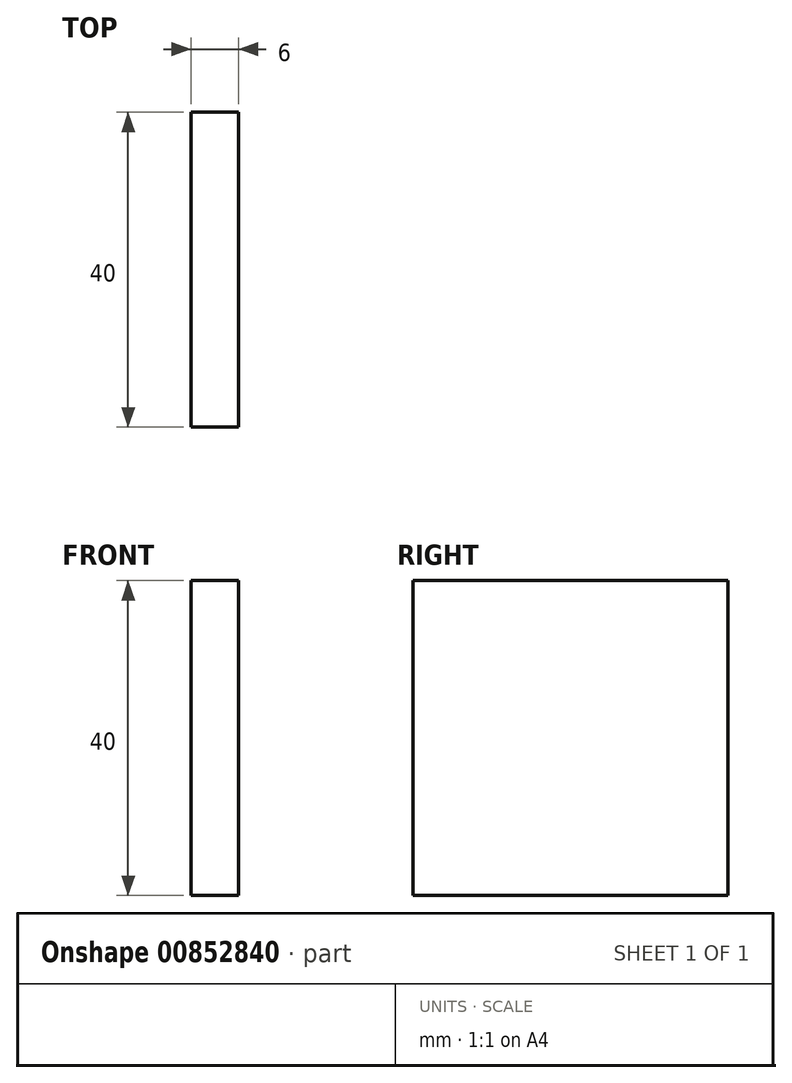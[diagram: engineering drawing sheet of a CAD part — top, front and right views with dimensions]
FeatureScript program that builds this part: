
annotation { "Feature Type Name" : "Feature", "Feature Type Description" : "" }
export const myFeature = defineFeature(function(context is Context, id is Id, definition is map)
    precondition{}
    {
        {
            var Q0;
            Q0=qCreatedBy(makeId("Right.planeOp"),FACE);
            var sketch = newSketch(context, id + "F0", { "sketchPlane" : qUnion([Q0])});
            skLineSegment(sketch, "E0.bottom", {"start": v(20, -20) * mm, "end": v(-20, -20) * mm});
            skLineSegment(sketch, "E0.top", {"start": v(20, 20) * mm, "end": v(-20, 20) * mm});
            skLineSegment(sketch, "E0.left", {"start": v(20, -20) * mm, "end": v(20, 20) * mm});
            skLineSegment(sketch, "E0.right", {"start": v(-20, -20) * mm, "end": v(-20, 20) * mm});
            skPoint(sketch, "E0.middle", {"position": v(0, 0) * mm});
            skSolve(sketch);
        }
        {
            var Q0;
            Q0=makeQuery(id+"F0.imprint","IMPRINT",FACE,{"disambiguationData":[TD([[makeQuery(id+"F0.imprint","IMPRINT",EDGE,{"derivedFrom":sQuery(id+"F0.wireOp",EDGE,"E0.bottom")}),-1.0]])]});
            extrude(context, id + "F1", {"entities" : qUnion([Q0]), "endBound" : BoundingType.SYMMETRIC, "depth" : 6 * mm, "offsetDistance" : 25 * mm});
        }
    });
